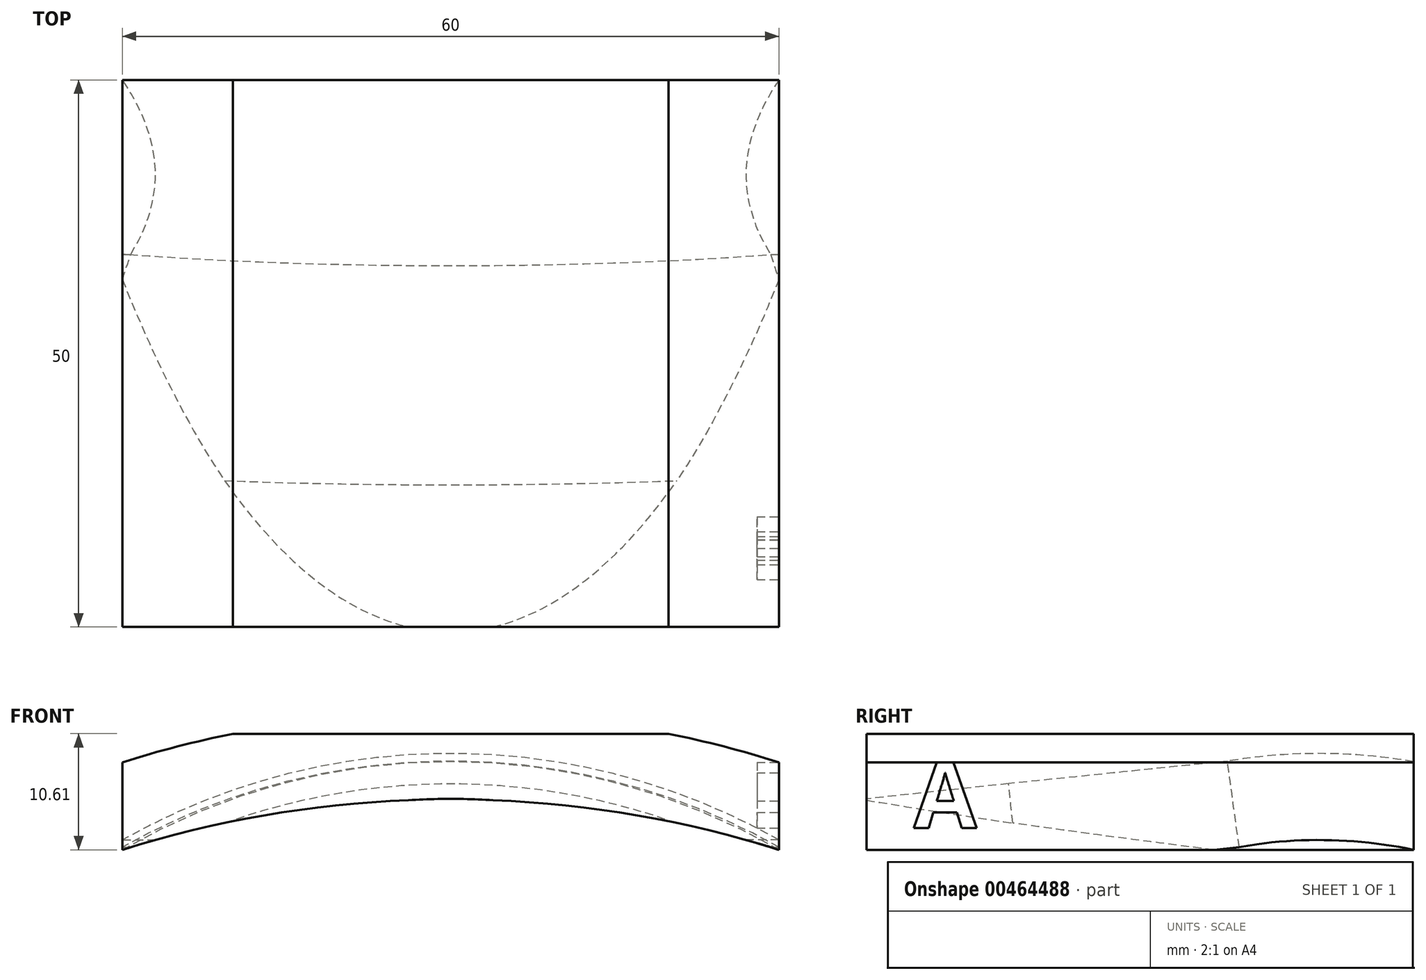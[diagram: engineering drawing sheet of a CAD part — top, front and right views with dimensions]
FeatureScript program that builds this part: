
annotation { "Feature Type Name" : "Feature", "Feature Type Description" : "" }
export const myFeature = defineFeature(function(context is Context, id is Id, definition is map)
    precondition{}
    {
        {
            var Q0;
            Q0=qCreatedBy(makeId("Front.planeOp"),FACE);
            var sketch = newSketch(context, id + "F0", { "sketchPlane" : qUnion([Q0])});
            skArc(sketch, "E0", {"start": v(60, 0) * mm, "mid": v(30, 4.6) * mm, "end": v(0, 0) * mm});
            skLineSegment(sketch, "E1", {"start": v(0, 0) * mm, "end": v(0, 8) * mm});
            skLineSegment(sketch, "E2", {"start": v(10.1, 10.6) * mm, "end": v(49.9, 10.6) * mm});
            skLineSegment(sketch, "E3", {"start": v(60, 8) * mm, "end": v(60, 0) * mm});
            skArc(sketch, "E4", {"start": v(60, 8) * mm, "mid": v(54.98, 9.43) * mm, "end": v(49.9, 10.6) * mm});
            skPoint(sketch, "E5.orphan", {"position": v(60, 10.6) * mm});
            skArc(sketch, "E6.trimOffspring", {"start": v(10.1, 10.6) * mm, "mid": v(5.02, 9.43) * mm, "end": v(0, 8) * mm});
            skSolve(sketch);
        }
        {
            var Q0;
            Q0 = qSketchRegion(id + "F0", true);
            extrude(context, id + "F1", {"entities" : qUnion([Q0]), "depth" : 25 * mm, "hasSecondDirection" : true, "secondDirectionOppositeDirection" : true, "secondDirectionDepth" : 25 * mm});
        }
        {
            var Q0;
            Q0=qCreatedBy(makeId("Right.planeOp"),FACE);
            cPlane(context, id + "F2", {"entities" : qUnion([Q0]), "cplaneType" : CPlaneType.OFFSET, "offset" : 30 * mm, "width" : 150 * mm, "height" : 150 * mm});
        }
        {
            var Q0;
            Q0=qCreatedBy(id+"F2.planeOp",FACE);
            var sketch = newSketch(context, id + "F3", { "sketchPlane" : qUnion([Q0])});
            skLineSegment(sketch, "E7", {"start": v(-29.46, 6) * mm, "end": v(30.4, 6) * mm, "construction": true});
            skLineSegment(sketch, "E8", {"start": v(25, 10.7) * mm, "end": v(25, 0) * mm, "construction": true});
            skArc(sketch, "E9", {"start": v(25, 8) * mm, "mid": v(16.5, 8.75) * mm, "end": v(8, 8.05) * mm});
            skPoint(sketch, "E9.endSnap0", {"position": v(0.47, 6) * mm});
            skLineSegment(sketch, "E10", {"start": v(8, 8.05) * mm, "end": v(-12, 6) * mm});
            skPoint(sketch, "E11.orphan", {"position": v(0, 6) * mm});
            skLineSegment(sketch, "E12", {"start": v(-12, 6) * mm, "end": v(-40, 3) * mm});
            skSolve(sketch);
        }
        {
            var Q0;
            Q0=makeQuery(id+"F1.opExtrude","CAP_FACE",FACE,{"disambiguationData":[OSD([sQuery(id+"F0.wireOp",EDGE,"E0"),sQuery(id+"F0.wireOp",EDGE,"E1"),sQuery(id+"F0.wireOp",EDGE,"E2"),sQuery(id+"F0.wireOp",EDGE,"E3"),sQuery(id+"F0.wireOp",EDGE,"E4"),sQuery(id+"F0.wireOp",EDGE,"E6.trimOffspring")])],"isStart":true});
            var sketch = newSketch(context, id + "F4", { "sketchPlane" : qUnion([Q0])});
            skArc(sketch, "E13", {"start": v(0, 0) * mm, "mid": v(-30, 8.05) * mm, "end": v(-60, 0) * mm});
            skLineSegment(sketch, "E14", {"start": v(-60, 0) * mm, "end": v(0, 0) * mm});
            skSolve(sketch);
        }
        {
            var Q0;
            Q0=makeQuery(id+"F4.imprint","IMPRINT",FACE,{"disambiguationData":[TD([[makeQuery(id+"F4.imprint","IMPRINT",EDGE,{"derivedFrom":sQuery(id+"F4.wireOp",EDGE,"E14")}),1.0]])]});
            var Q1;
            Q1=makeQuery(id+"F4.imprint","IMPRINT",FACE,{"disambiguationData":[TD([[makeQuery(id+"F4.imprint","IMPRINT",EDGE,{"derivedFrom":sQuery(id+"F4.wireOp",EDGE,"E13")}),1.0]])]});
            var Q2;
            Q2=sQuery(id+"F3.wireOp",EDGE,"E9");
            var Q3;
            Q3=sQuery(id+"F3.wireOp",EDGE,"E10");
            var Q4;
            Q4=sQuery(id+"F3.wireOp",EDGE,"E12");
            sweep(context, id + "F5", {"operationType" : NewBodyOperationType.REMOVE, "profiles" : qUnion([Q0, Q1]), "path" : qUnion([Q2, Q3, Q4])});
        }
        {
            var Q0;
            {var subQ1=sQuery(id+"F0.wireOp",EDGE,"E4");var subQ2=sQuery(id+"F0.wireOp",EDGE,"E3");Q0=makeQuery(id+"F5.boolean.opBoolean","SPLIT",FACE,{"disambiguationData":[TD([makeQuery(id+"F1.opExtrude","SWEPT_FACE",FACE,{"disambiguationData":[OSD([subQ1])]})])],"derivedFrom":makeQuery(id+"F1.opExtrude","SWEPT_FACE",FACE,{"disambiguationData":[OSD([subQ2])]})});}
            var sketch = newSketch(context, id + "F6", { "sketchPlane" : qUnion([Q0])});
            skText(sketch, "E15", { "text": "A", "fontName": "OpenSans-Bold.ttf"});
            const initialGuessF6  = {"E15": [-0.02068, 0.002, 1, 0, 0.006]};
            skSetInitialGuess(sketch, initialGuessF6);
            skSolve(sketch);
        }
        {
            var Q0;
            Q0 = qSketchRegion(id + "F6", true);
            extrude(context, id + "F7", {"entities" : qUnion([Q0]), "operationType" : NewBodyOperationType.REMOVE, "oppositeDirection" : true, "depth" : 2 * mm});
        }
    });
